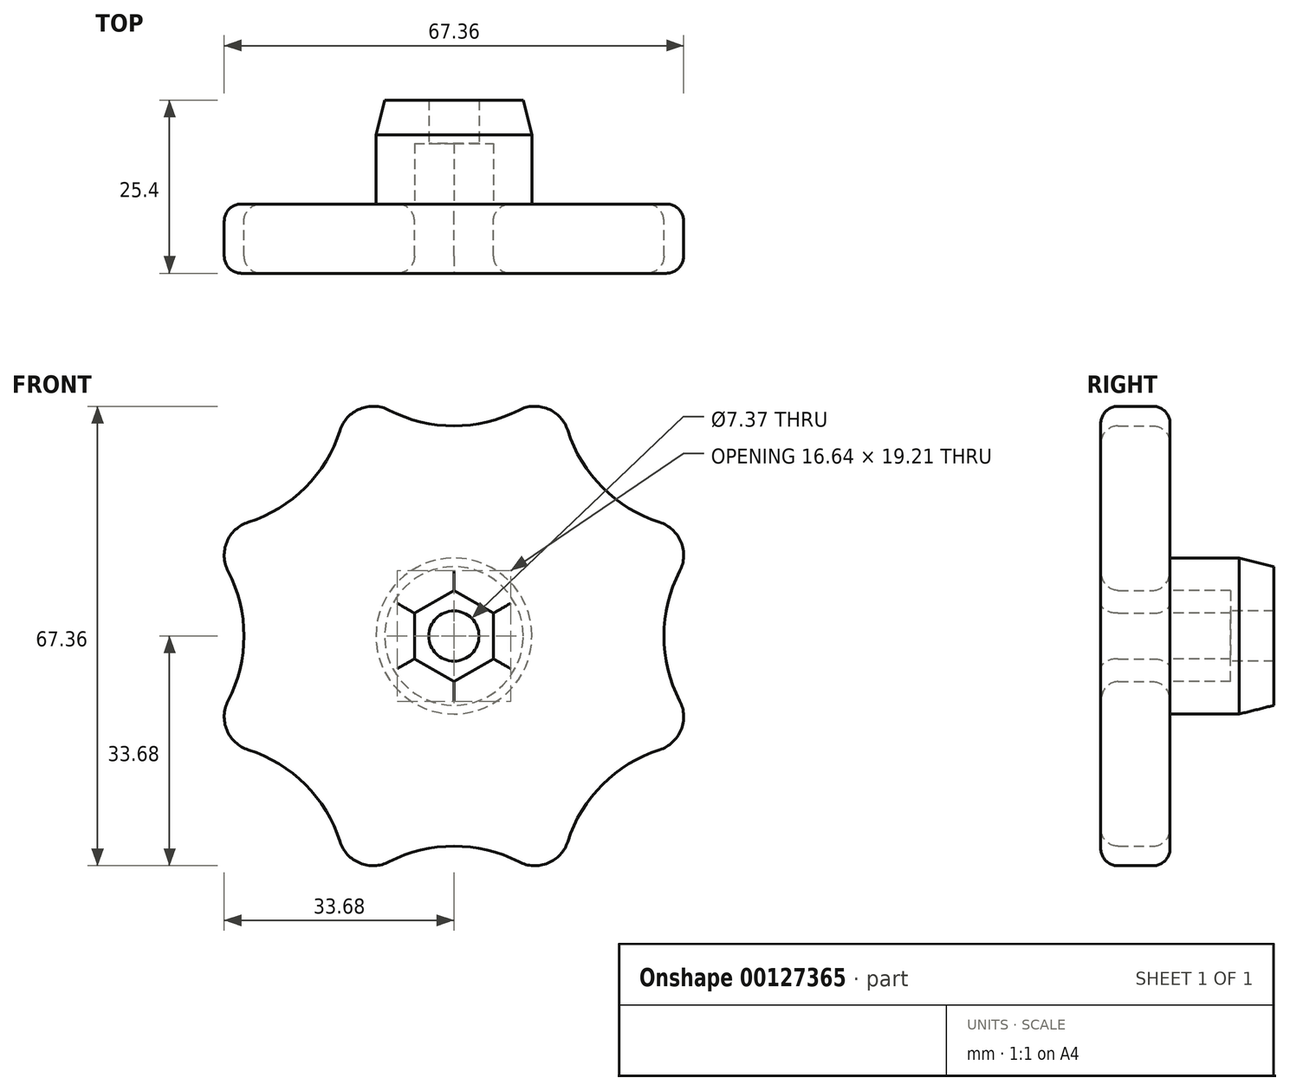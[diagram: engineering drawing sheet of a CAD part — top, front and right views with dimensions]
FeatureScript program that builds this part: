
annotation { "Feature Type Name" : "Feature", "Feature Type Description" : "" }
export const myFeature = defineFeature(function(context is Context, id is Id, definition is map)
    precondition{}
    {
        {
            var Q0;
            Q0=qCreatedBy(makeId("Front.planeOp"),FACE);
            var sketch = newSketch(context, id + "F0", { "sketchPlane" : qUnion([Q0])});
            skCircle(sketch, "E0", {"center": v(0, 0) * mm, "radius": 11.43 * mm});
            skSolve(sketch);
        }
        {
            var Q0;
            {var subQ0=sQuery(id+"F0.wireOp",EDGE,"E0");var subQ1=makeQuery(id+"F0.imprint","INTERSECT",VERTEX,{"derivedFrom":[subQ0,sQuery(id+"F0.wireOp",EDGE,"ea245839-a498-4638-985b-73fae0246c39")]});Q0=makeQuery(id+"F0.imprint","IMPRINT",FACE,{"disambiguationData":[TD([[makeQuery(id+"F0.imprint","IMPRINT",EDGE,{"disambiguationData":[TD([[subQ1,-1.0]])],"derivedFrom":subQ0}),1.0]])]});}
            var Q1;
            Q1=makeQuery(id+"F0.imprint","IMPRINT",FACE,{"disambiguationData":[TD([[makeQuery(id+"F0.imprint","IMPRINT",EDGE,{"derivedFrom":sQuery(id+"F0.wireOp",EDGE,"2dcc8b00-aa93-42b5-8a72-6d1d4eab4258")}),1.0]])]});
            extrude(context, id + "F1", {"entities" : qUnion([Q0, Q1]), "offsetDistance" : 25.4 * mm, "depth" : 15.24 * mm});
        }
        {
            var Q0;
            Q0=makeQuery(id+"F1.opExtrude","CAP_FACE",FACE,{"disambiguationData":[OSD([sQuery(id+"F0.wireOp",EDGE,"E0"),sQuery(id+"F0.wireOp",EDGE,"2dcc8b00-aa93-42b5-8a72-6d1d4eab4258"),sQuery(id+"F0.wireOp",EDGE,"ea245839-a498-4638-985b-73fae0246c39"),sQuery(id+"F0.wireOp",EDGE,"28ef0078-34b0-4df2-9f13-6cd2cfbab48c0.MirrorCS"),sQuery(id+"F0.wireOp",EDGE,"f54b358c-e5d3-4f08-8e52-d21b7307fad60.MirrorCS")])],"isStart":false});
            var sketch = newSketch(context, id + "F2", { "sketchPlane" : qUnion([Q0])});
            skCircle(sketch, "E1.cCircle", {"center": v(0, 0) * mm, "radius": 5.78 * mm, "construction": true});
            skLineSegment(sketch, "E1.0", {"start": v(5.78, 3.34) * mm, "end": v(5.78, -3.34) * mm});
            skLineSegment(sketch, "E1.1", {"start": v(5.78, -3.34) * mm, "end": v(0, -6.67) * mm});
            skLineSegment(sketch, "E1.2", {"start": v(0, -6.67) * mm, "end": v(-5.78, -3.34) * mm});
            skLineSegment(sketch, "E1.3", {"start": v(-5.78, -3.34) * mm, "end": v(-5.78, 3.34) * mm});
            skLineSegment(sketch, "E1.4", {"start": v(-5.78, 3.34) * mm, "end": v(0, 6.67) * mm});
            skLineSegment(sketch, "E1.5", {"start": v(0, 6.67) * mm, "end": v(5.78, 3.34) * mm});
            skPoint(sketch, "E1.0.midPoint", {"position": v(5.78, 0) * mm});
            skSolve(sketch);
        }
        {
            var Q0;
            Q0=makeQuery(id+"F2.imprint","IMPRINT",FACE,{"disambiguationData":[TD([[makeQuery(id+"F2.imprint","IMPRINT",EDGE,{"derivedFrom":sQuery(id+"F2.wireOp",EDGE,"E1.0")}),-1.0]])]});
            extrude(context, id + "F3", {"entities" : qUnion([Q0]), "operationType" : NewBodyOperationType.REMOVE, "oppositeDirection" : true, "depth" : 8.9 * mm});
        }
        {
            var Q0;
            Q0=makeQuery(id+"F3.boolean.opBoolean","COPY",FACE,{"derivedFrom":makeQuery(id+"F3.opExtrude","CAP_FACE",FACE,{"disambiguationData":[OSD([sQuery(id+"F2.wireOp",EDGE,"E1.0"),sQuery(id+"F2.wireOp",EDGE,"E1.1"),sQuery(id+"F2.wireOp",EDGE,"E1.2"),sQuery(id+"F2.wireOp",EDGE,"E1.3"),sQuery(id+"F2.wireOp",EDGE,"E1.4"),sQuery(id+"F2.wireOp",EDGE,"E1.5")])],"isStart":false})});
            var sketch = newSketch(context, id + "F4", { "sketchPlane" : qUnion([Q0])});
            skCircle(sketch, "E2", {"center": v(0, 0) * mm, "radius": 3.68 * mm});
            skSolve(sketch);
        }
        {
            var Q0;
            Q0=makeQuery(id+"F4.imprint","IMPRINT",FACE,{"disambiguationData":[TD([[makeQuery(id+"F4.imprint","IMPRINT",EDGE,{"derivedFrom":sQuery(id+"F4.wireOp",EDGE,"E2")}),1.0]])]});
            extrude(context, id + "F5", {"entities" : qUnion([Q0]), "operationType" : NewBodyOperationType.REMOVE, "endBound" : BoundingType.THROUGH_ALL, "oppositeDirection" : true, "offsetDistance" : 25.4 * mm, "depth" : 25.4 * mm});
        }
        {
            var Q0;
            Q0=makeQuery(id+"F1.opExtrude","CAP_EDGE",EDGE,{"disambiguationData":[OSD([sQuery(id+"F0.wireOp",EDGE,"E0")])],"isStart":true});
            chamfer(context, id + "F6", {"entities" : qUnion([Q0]), "chamferType" : ChamferType.TWO_OFFSETS, "width1" : 5.08 * mm, "oppositeDirection" : false, "width2" : 1.27 * mm, "tangentPropagation" : true});
        }
        {
            var Q0;
            Q0=makeQuery(id+"F1.opExtrude","CAP_FACE",FACE,{"disambiguationData":[OSD([sQuery(id+"F0.wireOp",EDGE,"E0")])],"isStart":false});
            var sketch = newSketch(context, id + "F7", { "sketchPlane" : qUnion([Q0])});
            skCircle(sketch, "E3.cCircle", {"center": v(0, 0) * mm, "radius": 38.1 * mm, "construction": true});
            skLineSegment(sketch, "E3.0", {"start": v(38.1, 15.78) * mm, "end": v(38.1, -15.78) * mm});
            skLineSegment(sketch, "E3.1", {"start": v(38.1, -15.78) * mm, "end": v(15.78, -38.1) * mm});
            skLineSegment(sketch, "E3.2", {"start": v(15.78, -38.1) * mm, "end": v(-15.78, -38.1) * mm});
            skLineSegment(sketch, "E3.3", {"start": v(-15.78, -38.1) * mm, "end": v(-38.1, -15.78) * mm});
            skLineSegment(sketch, "E3.4", {"start": v(-38.1, -15.78) * mm, "end": v(-38.1, 15.78) * mm});
            skLineSegment(sketch, "E3.5", {"start": v(-38.1, 15.78) * mm, "end": v(-15.78, 38.1) * mm});
            skLineSegment(sketch, "E3.6", {"start": v(-15.78, 38.1) * mm, "end": v(15.78, 38.1) * mm});
            skLineSegment(sketch, "E3.7", {"start": v(15.78, 38.1) * mm, "end": v(38.1, 15.78) * mm});
            skPoint(sketch, "E3.0.midPoint", {"position": v(38.1, 0) * mm});
            skArc(sketch, "E4", {"start": v(-38.1, 15.78) * mm, "mid": v(-21.78, 21.78) * mm, "end": v(-15.78, 38.1) * mm});
            skArc(sketch, "E5.1.0", {"start": v(-38.1, -15.78) * mm, "mid": v(-30.8, 0) * mm, "end": v(-38.1, 15.78) * mm});
            skArc(sketch, "E5.2.0", {"start": v(-15.78, -38.1) * mm, "mid": v(-21.78, -21.78) * mm, "end": v(-38.1, -15.78) * mm});
            skArc(sketch, "E5.3.0", {"start": v(15.78, -38.1) * mm, "mid": v(0, -30.8) * mm, "end": v(-15.78, -38.1) * mm});
            skArc(sketch, "E5.4.0", {"start": v(38.1, -15.78) * mm, "mid": v(21.78, -21.78) * mm, "end": v(15.78, -38.1) * mm});
            skArc(sketch, "E5.5.0", {"start": v(38.1, 15.78) * mm, "mid": v(30.8, 0) * mm, "end": v(38.1, -15.78) * mm});
            skArc(sketch, "E5.6.0", {"start": v(15.78, 38.1) * mm, "mid": v(21.78, 21.78) * mm, "end": v(38.1, 15.78) * mm});
            skArc(sketch, "E5.7.0", {"start": v(-15.78, 38.1) * mm, "mid": v(0, 30.8) * mm, "end": v(15.78, 38.1) * mm});
            skSolve(sketch);
        }
        {
            var Q0;
            Q0=makeQuery(id+"F7.imprint","IMPRINT",FACE,{"disambiguationData":[TD([[makeQuery(id+"F7.imprint","IMPRINT",EDGE,{"derivedFrom":sQuery(id+"F7.wireOp",EDGE,"E4")}),-1.0]])]});
            var Q1;
            Q1=makeQuery(id+"F7.imprint","IMPRINT",FACE,{"disambiguationData":[TD([[makeQuery(id+"F7.imprint","IMPRINT",EDGE,{"derivedFrom":makeQuery(id+"F1.opExtrude","CAP_EDGE",EDGE,{"disambiguationData":[OSD([sQuery(id+"F0.wireOp",EDGE,"E0")])],"isStart":false})}),1.0]])]});
            extrude(context, id + "F8", {"entities" : qUnion([Q0, Q1]), "depth" : 10.16 * mm, "offsetDistance" : 25.4 * mm});
        }
        {
            var Q0;
            Q0=makeQuery(id+"F8.opExtrude","SWEPT_EDGE",EDGE,{"disambiguationData":[OSD([sQuery(id+"F7.wireOp",EDGE,"E3.5"),sQuery(id+"F7.wireOp",EDGE,"E3.6"),sQuery(id+"F7.wireOp",EDGE,"E4"),sQuery(id+"F7.wireOp",EDGE,"E5.7.0")])]});
            var Q1;
            Q1=makeQuery(id+"F8.opExtrude","SWEPT_EDGE",EDGE,{"disambiguationData":[OSD([sQuery(id+"F7.wireOp",EDGE,"E3.4"),sQuery(id+"F7.wireOp",EDGE,"E3.5"),sQuery(id+"F7.wireOp",EDGE,"E4"),sQuery(id+"F7.wireOp",EDGE,"E5.1.0")])]});
            var Q2;
            Q2=makeQuery(id+"F8.opExtrude","SWEPT_EDGE",EDGE,{"disambiguationData":[OSD([sQuery(id+"F7.wireOp",EDGE,"E3.3"),sQuery(id+"F7.wireOp",EDGE,"E3.4"),sQuery(id+"F7.wireOp",EDGE,"E5.1.0"),sQuery(id+"F7.wireOp",EDGE,"E5.2.0")])]});
            var Q3;
            Q3=makeQuery(id+"F8.opExtrude","SWEPT_EDGE",EDGE,{"disambiguationData":[OSD([sQuery(id+"F7.wireOp",EDGE,"E3.2"),sQuery(id+"F7.wireOp",EDGE,"E3.3"),sQuery(id+"F7.wireOp",EDGE,"E5.2.0"),sQuery(id+"F7.wireOp",EDGE,"E5.3.0")])]});
            var Q4;
            Q4=makeQuery(id+"F8.opExtrude","SWEPT_EDGE",EDGE,{"disambiguationData":[OSD([sQuery(id+"F7.wireOp",EDGE,"E3.1"),sQuery(id+"F7.wireOp",EDGE,"E3.2"),sQuery(id+"F7.wireOp",EDGE,"E5.3.0"),sQuery(id+"F7.wireOp",EDGE,"E5.4.0")])]});
            var Q5;
            Q5=makeQuery(id+"F8.opExtrude","SWEPT_EDGE",EDGE,{"disambiguationData":[OSD([sQuery(id+"F7.wireOp",EDGE,"E3.0"),sQuery(id+"F7.wireOp",EDGE,"E3.1"),sQuery(id+"F7.wireOp",EDGE,"E5.4.0"),sQuery(id+"F7.wireOp",EDGE,"E5.5.0")])]});
            var Q6;
            Q6=makeQuery(id+"F8.opExtrude","SWEPT_EDGE",EDGE,{"disambiguationData":[OSD([sQuery(id+"F7.wireOp",EDGE,"E3.0"),sQuery(id+"F7.wireOp",EDGE,"E3.7"),sQuery(id+"F7.wireOp",EDGE,"E5.5.0"),sQuery(id+"F7.wireOp",EDGE,"E5.6.0")])]});
            var Q7;
            Q7=makeQuery(id+"F8.opExtrude","SWEPT_EDGE",EDGE,{"disambiguationData":[OSD([sQuery(id+"F7.wireOp",EDGE,"E3.6"),sQuery(id+"F7.wireOp",EDGE,"E3.7"),sQuery(id+"F7.wireOp",EDGE,"E5.6.0"),sQuery(id+"F7.wireOp",EDGE,"E5.7.0")])]});
            fillet(context, id + "F9", {"entities" : qUnion([Q0, Q1, Q2, Q3, Q4, Q5, Q6, Q7]), "radius" : 5.08 * mm, "tangentPropagation" : true, "allowEdgeOverflow" : false});
        }
        {
            var Q0;
            Q0=makeQuery(id+"F8.opExtrude","CAP_FACE",FACE,{"disambiguationData":[OSD([sQuery(id+"F2.wireOp",EDGE,"E1.0"),sQuery(id+"F2.wireOp",EDGE,"E1.1"),sQuery(id+"F2.wireOp",EDGE,"E1.2"),sQuery(id+"F2.wireOp",EDGE,"E1.3"),sQuery(id+"F2.wireOp",EDGE,"E1.4"),sQuery(id+"F2.wireOp",EDGE,"E1.5"),sQuery(id+"F7.wireOp",EDGE,"E4"),sQuery(id+"F7.wireOp",EDGE,"E5.1.0"),sQuery(id+"F7.wireOp",EDGE,"E5.2.0"),sQuery(id+"F7.wireOp",EDGE,"E5.3.0"),sQuery(id+"F7.wireOp",EDGE,"E5.4.0"),sQuery(id+"F7.wireOp",EDGE,"E5.5.0"),sQuery(id+"F7.wireOp",EDGE,"E5.6.0"),sQuery(id+"F7.wireOp",EDGE,"E5.7.0")])],"isStart":false});
            var Q1;
            Q1=makeQuery(id+"F8.opExtrude","CAP_FACE",FACE,{"disambiguationData":[OSD([sQuery(id+"F2.wireOp",EDGE,"E1.0"),sQuery(id+"F2.wireOp",EDGE,"E1.1"),sQuery(id+"F2.wireOp",EDGE,"E1.2"),sQuery(id+"F2.wireOp",EDGE,"E1.3"),sQuery(id+"F2.wireOp",EDGE,"E1.4"),sQuery(id+"F2.wireOp",EDGE,"E1.5"),sQuery(id+"F7.wireOp",EDGE,"E4"),sQuery(id+"F7.wireOp",EDGE,"E5.1.0"),sQuery(id+"F7.wireOp",EDGE,"E5.2.0"),sQuery(id+"F7.wireOp",EDGE,"E5.3.0"),sQuery(id+"F7.wireOp",EDGE,"E5.4.0"),sQuery(id+"F7.wireOp",EDGE,"E5.5.0"),sQuery(id+"F7.wireOp",EDGE,"E5.6.0"),sQuery(id+"F7.wireOp",EDGE,"E5.7.0")])],"isStart":true});
            fillet(context, id + "F10", {"entities" : qUnion([Q0, Q1]), "radius" : 2.54 * mm, "tangentPropagation" : true, "allowEdgeOverflow" : false});
        }
    });
